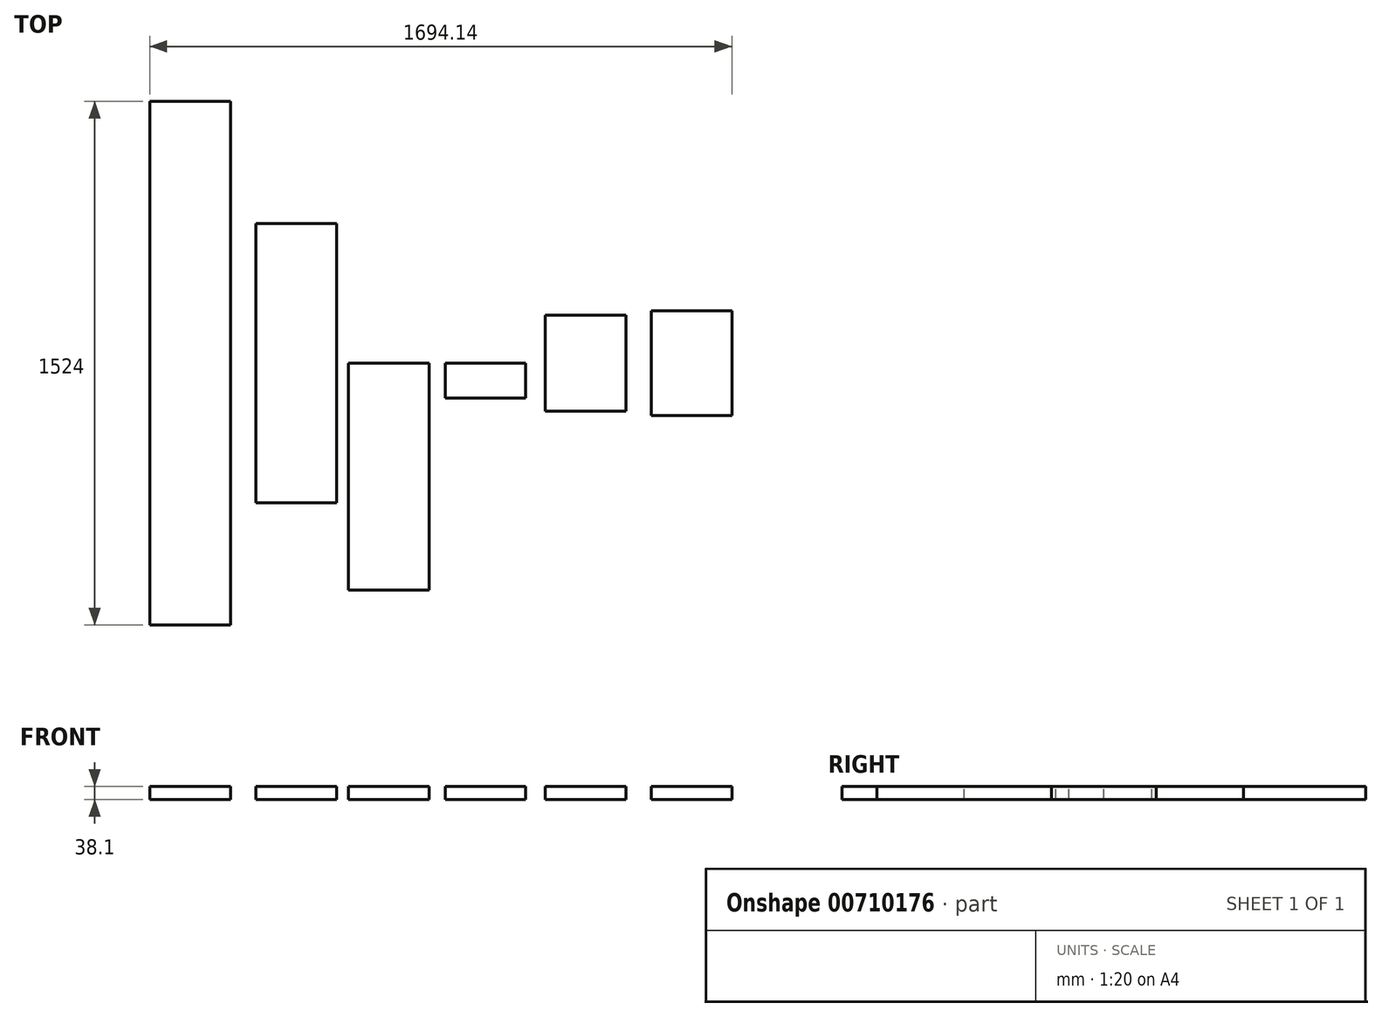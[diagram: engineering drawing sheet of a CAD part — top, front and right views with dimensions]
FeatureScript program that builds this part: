
annotation { "Feature Type Name" : "Feature", "Feature Type Description" : "" }
export const myFeature = defineFeature(function(context is Context, id is Id, definition is map)
    precondition{}
    {
        {
            var Q0;
            Q0=qCreatedBy(makeId("Front.planeOp"),FACE);
            var sketch = newSketch(context, id + "F0", { "sketchPlane" : qUnion([Q0])});
            skLineSegment(sketch, "E0.bottom", {"start": v(117.48, -19.05) * mm, "end": v(-117.48, -19.05) * mm});
            skLineSegment(sketch, "E0.top", {"start": v(117.48, 19.05) * mm, "end": v(-117.48, 19.05) * mm});
            skLineSegment(sketch, "E0.left", {"start": v(117.48, -19.05) * mm, "end": v(117.48, 19.05) * mm});
            skLineSegment(sketch, "E0.right", {"start": v(-117.48, -19.05) * mm, "end": v(-117.48, 19.05) * mm});
            skPoint(sketch, "E0.middle", {"position": v(0, 0) * mm});
            skSolve(sketch);
        }
        {
            var Q0;
            Q0 = qSketchRegion(id + "F0", true);
            extrude(context, id + "F1", {"entities" : qUnion([Q0]), "endBound" : BoundingType.SYMMETRIC, "depth" : 1524 * mm, "offsetDistance" : 25 * mm});
        }
        {
            var Q0;
            Q0=qCreatedBy(makeId("Front.planeOp"),FACE);
            var sketch = newSketch(context, id + "F2", { "sketchPlane" : qUnion([Q0])});
            skLineSegment(sketch, "E1.bottom", {"start": v(426.44, -19.05) * mm, "end": v(191.49, -19.05) * mm});
            skLineSegment(sketch, "E1.top", {"start": v(426.44, 19.05) * mm, "end": v(191.49, 19.05) * mm});
            skLineSegment(sketch, "E1.left", {"start": v(426.44, -19.05) * mm, "end": v(426.44, 19.05) * mm});
            skLineSegment(sketch, "E1.right", {"start": v(191.49, -19.05) * mm, "end": v(191.49, 19.05) * mm});
            skPoint(sketch, "E1.middle", {"position": v(308.96, 0) * mm});
            skSolve(sketch);
        }
        {
            var Q0;
            Q0 = qSketchRegion(id + "F2", true);
            extrude(context, id + "F3", {"entities" : qUnion([Q0]), "endBound" : BoundingType.SYMMETRIC, "depth" : 812.8 * mm, "offsetDistance" : 25 * mm});
        }
        {
            var Q0;
            Q0=qCreatedBy(makeId("Front.planeOp"),FACE);
            var sketch = newSketch(context, id + "F4", { "sketchPlane" : qUnion([Q0])});
            skLineSegment(sketch, "E2.bottom", {"start": v(695.48, -19.05) * mm, "end": v(460.53, -19.05) * mm});
            skLineSegment(sketch, "E2.top", {"start": v(695.48, 19.05) * mm, "end": v(460.53, 19.05) * mm});
            skLineSegment(sketch, "E2.left", {"start": v(695.48, -19.05) * mm, "end": v(695.48, 19.05) * mm});
            skLineSegment(sketch, "E2.right", {"start": v(460.53, -19.05) * mm, "end": v(460.53, 19.05) * mm});
            skPoint(sketch, "E2.middle", {"position": v(578, 0) * mm});
            skSolve(sketch);
        }
        {
            var Q0;
            Q0 = qSketchRegion(id + "F4", true);
            extrude(context, id + "F5", {"entities" : qUnion([Q0]), "depth" : 660.4 * mm, "offsetDistance" : 25 * mm});
        }
        {
            var Q0;
            Q0=qCreatedBy(makeId("Front.planeOp"),FACE);
            var sketch = newSketch(context, id + "F6", { "sketchPlane" : qUnion([Q0])});
            skLineSegment(sketch, "E3.bottom", {"start": v(977.1, -19.05) * mm, "end": v(742.15, -19.05) * mm});
            skLineSegment(sketch, "E3.top", {"start": v(977.1, 19.05) * mm, "end": v(742.15, 19.05) * mm});
            skLineSegment(sketch, "E3.left", {"start": v(977.1, -19.05) * mm, "end": v(977.1, 19.05) * mm});
            skLineSegment(sketch, "E3.right", {"start": v(742.15, -19.05) * mm, "end": v(742.15, 19.05) * mm});
            skPoint(sketch, "E3.middle", {"position": v(859.62, 0) * mm});
            skSolve(sketch);
        }
        {
            var Q0;
            Q0 = qSketchRegion(id + "F6", true);
            extrude(context, id + "F7", {"entities" : qUnion([Q0]), "depth" : 101.6 * mm, "offsetDistance" : 25 * mm});
        }
        {
            var Q0;
            Q0=qCreatedBy(makeId("Front.planeOp"),FACE);
            var sketch = newSketch(context, id + "F8", { "sketchPlane" : qUnion([Q0])});
            skLineSegment(sketch, "E4.bottom", {"start": v(1268.86, -19.05) * mm, "end": v(1033.91, -19.05) * mm});
            skLineSegment(sketch, "E4.top", {"start": v(1268.86, 19.05) * mm, "end": v(1033.91, 19.05) * mm});
            skLineSegment(sketch, "E4.left", {"start": v(1268.86, -19.05) * mm, "end": v(1268.86, 19.05) * mm});
            skLineSegment(sketch, "E4.right", {"start": v(1033.91, -19.05) * mm, "end": v(1033.91, 19.05) * mm});
            skPoint(sketch, "E4.middle", {"position": v(1151.39, 0) * mm});
            skSolve(sketch);
        }
        {
            var Q0;
            Q0 = qSketchRegion(id + "F8", true);
            extrude(context, id + "F9", {"entities" : qUnion([Q0]), "endBound" : BoundingType.SYMMETRIC, "depth" : 279.4 * mm, "offsetDistance" : 25 * mm});
        }
        {
            var Q0;
            Q0=qCreatedBy(makeId("Front.planeOp"),FACE);
            var sketch = newSketch(context, id + "F10", { "sketchPlane" : qUnion([Q0])});
            skLineSegment(sketch, "E5.bottom", {"start": v(1576.67, -19.05) * mm, "end": v(1341.72, -19.05) * mm});
            skLineSegment(sketch, "E5.top", {"start": v(1576.67, 19.05) * mm, "end": v(1341.72, 19.05) * mm});
            skLineSegment(sketch, "E5.left", {"start": v(1576.67, -19.05) * mm, "end": v(1576.67, 19.05) * mm});
            skLineSegment(sketch, "E5.right", {"start": v(1341.72, -19.05) * mm, "end": v(1341.72, 19.05) * mm});
            skPoint(sketch, "E5.middle", {"position": v(1459.2, 0) * mm});
            skSolve(sketch);
        }
        {
            var Q0;
            Q0 = qSketchRegion(id + "F10", true);
            extrude(context, id + "F11", {"entities" : qUnion([Q0]), "endBound" : BoundingType.SYMMETRIC, "depth" : 304.8 * mm, "offsetDistance" : 25 * mm});
        }
    });
